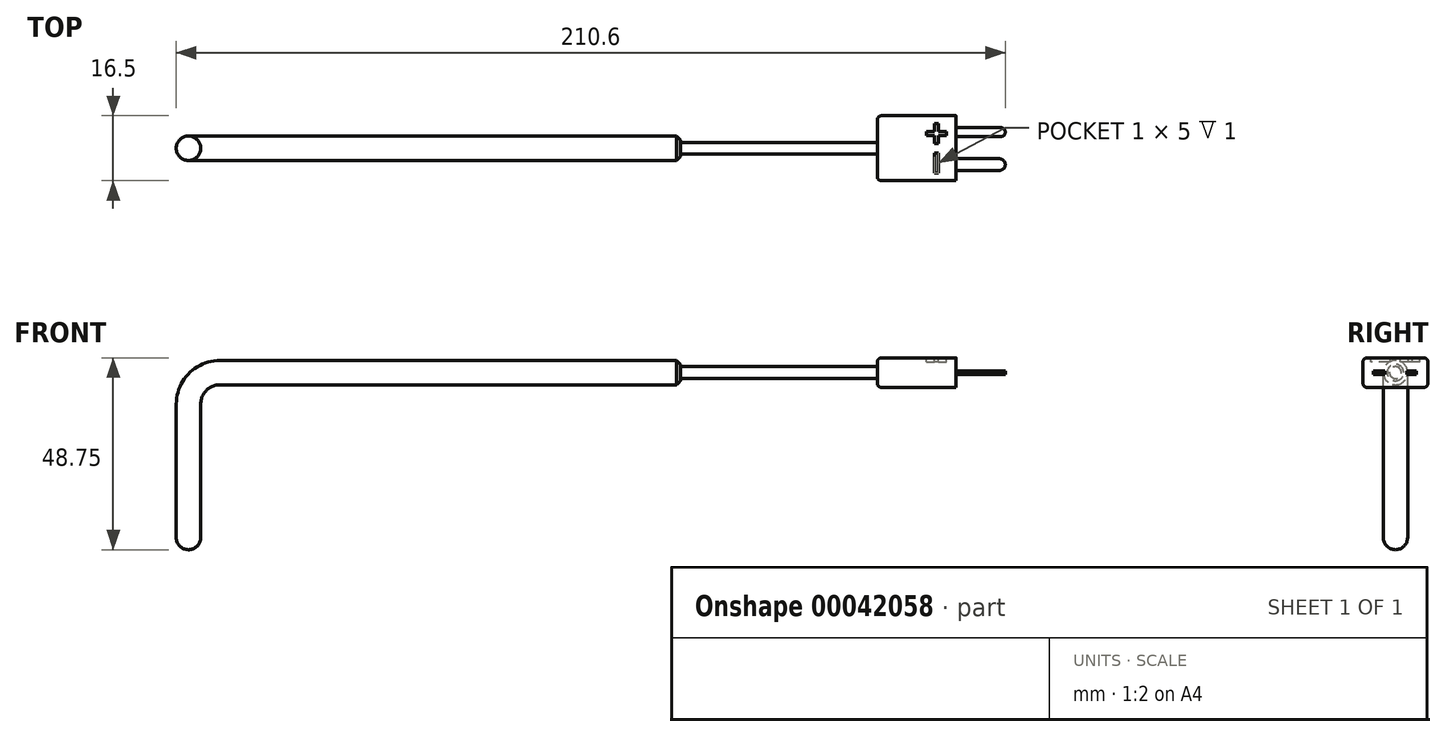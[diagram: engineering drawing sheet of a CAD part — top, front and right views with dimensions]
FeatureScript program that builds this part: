
annotation { "Feature Type Name" : "Feature", "Feature Type Description" : "" }
export const myFeature = defineFeature(function(context is Context, id is Id, definition is map)
    precondition{}
    {
        {
            var Q0;
            Q0=qCreatedBy(makeId("Front.planeOp"),FACE);
            var sketch = newSketch(context, id + "F0", { "sketchPlane" : qUnion([Q0])});
            skLineSegment(sketch, "E0", {"start": v(0, 0) * mm, "end": v(0, 37) * mm});
            skLineSegment(sketch, "E1", {"start": v(8, 45) * mm, "end": v(125, 45) * mm});
            skPoint(sketch, "E2.visualSharp", {"position": v(0, 45) * mm});
            skArc(sketch, "E2.filletArc", {"start": v(8, 45) * mm, "mid": v(2.34, 42.66) * mm, "end": v(0, 37) * mm});
            skSolve(sketch);
        }
        {
            var Q0;
            Q0=qCreatedBy(makeId("Top.planeOp"),FACE);
            var sketch = newSketch(context, id + "F1", { "sketchPlane" : qUnion([Q0])});
            skCircle(sketch, "E3", {"center": v(0, 0) * mm, "radius": 3.1 * mm});
            skSolve(sketch);
        }
        {
            var Q0;
            Q0=makeQuery(id+"F1.imprint","IMPRINT",FACE,{"disambiguationData":[TD([[makeQuery(id+"F1.imprint","IMPRINT",EDGE,{"derivedFrom":sQuery(id+"F1.wireOp",EDGE,"E3")}),1.0]])]});
            var Q1;
            Q1=sQuery(id+"F0.wireOp",EDGE,"E0");
            var Q2;
            Q2=sQuery(id+"F0.wireOp",EDGE,"E2.filletArc");
            var Q3;
            Q3=sQuery(id+"F0.wireOp",EDGE,"E1");
            sweep(context, id + "F2", {"profiles" : qUnion([Q0]), "path" : qUnion([Q1, Q2, Q3])});
        }
        {
            var Q0;
            Q0=makeQuery(id+"F2.opSweep","CAP_FACE",FACE,{"disambiguationData":[OSD([sQuery(id+"F0.wireOp",VERTEX,"E0.start"),sQuery(id+"F1.wireOp",EDGE,"E3")])],"isStart":true});
            fillet(context, id + "F3", {"entities" : qUnion([Q0]), "radius" : 3.1 * mm, "tangentPropagation" : true, "allowEdgeOverflow" : false});
        }
        {
            var Q0;
            Q0=makeQuery(id+"F2.opSweep","CAP_FACE",FACE,{"disambiguationData":[OSD([sQuery(id+"F0.wireOp",VERTEX,"E1.end"),sQuery(id+"F1.wireOp",EDGE,"E3")])],"isStart":false});
            var sketch = newSketch(context, id + "F4", { "sketchPlane" : qUnion([Q0])});
            skCircle(sketch, "E4", {"center": v(0, 45) * mm, "radius": 1.5 * mm});
            skSolve(sketch);
        }
        {
            var Q0;
            Q0=makeQuery(id+"F4.imprint","IMPRINT",FACE,{"disambiguationData":[TD([[makeQuery(id+"F4.imprint","IMPRINT",EDGE,{"derivedFrom":sQuery(id+"F4.wireOp",EDGE,"E4")}),1.0]])]});
            extrude(context, id + "F5", {"entities" : qUnion([Q0]), "depth" : 50 * mm});
        }
        {
            var Q0;
            Q0=makeQuery(id+"F2.opSweep","CAP_EDGE",EDGE,{"disambiguationData":[OSD([sQuery(id+"F0.wireOp",VERTEX,"E1.end"),sQuery(id+"F1.wireOp",EDGE,"E3")])],"isStart":false});
            chamfer(context, id + "F6", {"entities" : qUnion([Q0]), "width" : 1 * mm, "tangentPropagation" : true});
        }
        {
            var Q0;
            Q0=makeQuery(id+"F5.opExtrude","CAP_FACE",FACE,{"disambiguationData":[OSD([sQuery(id+"F4.wireOp",EDGE,"E4")])],"isStart":false});
            var sketch = newSketch(context, id + "F7", { "sketchPlane" : qUnion([Q0])});
            skLineSegment(sketch, "E5.rect.bottom", {"start": v(8.25, 48.75) * mm, "end": v(-8.25, 48.75) * mm});
            skLineSegment(sketch, "E5.rect.top", {"start": v(8.25, 41.25) * mm, "end": v(-8.25, 41.25) * mm});
            skLineSegment(sketch, "E5.rect.left", {"start": v(8.25, 48.75) * mm, "end": v(8.25, 41.25) * mm});
            skLineSegment(sketch, "E5.rect.right", {"start": v(-8.25, 48.75) * mm, "end": v(-8.25, 41.25) * mm});
            skPoint(sketch, "E5.rect.middle", {"position": v(0, 45) * mm});
            skSolve(sketch);
        }
        {
            var Q0;
            Q0=makeQuery(id+"F7.imprint","IMPRINT",FACE,{"disambiguationData":[TD([[makeQuery(id+"F7.imprint","IMPRINT",EDGE,{"derivedFrom":makeQuery(id+"F5.opExtrude","CAP_EDGE",EDGE,{"disambiguationData":[OSD([sQuery(id+"F4.wireOp",EDGE,"E4")])],"isStart":false})}),1.0]])]});
            var Q1;
            Q1=makeQuery(id+"F7.imprint","IMPRINT",FACE,{"disambiguationData":[TD([[makeQuery(id+"F7.imprint","IMPRINT",EDGE,{"derivedFrom":sQuery(id+"F7.wireOp",EDGE,"E5.rect.bottom")}),1.0]])]});
            extrude(context, id + "F8", {"entities" : qUnion([Q0, Q1]), "operationType" : NewBodyOperationType.ADD, "depth" : 20 * mm});
        }
        {
            var Q0;
            Q0=makeQuery(id+"F8.opExtrude","CAP_FACE",FACE,{"disambiguationData":[OSD([sQuery(id+"F7.wireOp",EDGE,"E5.rect.bottom"),sQuery(id+"F7.wireOp",EDGE,"E5.rect.top"),sQuery(id+"F7.wireOp",EDGE,"E5.rect.left"),sQuery(id+"F7.wireOp",EDGE,"E5.rect.right")])],"isStart":false});
            var sketch = newSketch(context, id + "F9", { "sketchPlane" : qUnion([Q0])});
            skLineSegment(sketch, "E6", {"start": v(-8.25, 45) * mm, "end": v(8.25, 45) * mm, "construction": true});
            skLineSegment(sketch, "E7", {"start": v(0, 48.75) * mm, "end": v(0, 41.25) * mm, "construction": true});
            skLineSegment(sketch, "E8.rect.bottom", {"start": v(-2.65, 45.45) * mm, "end": v(-5.65, 45.45) * mm});
            skLineSegment(sketch, "E8.rect.top", {"start": v(-2.65, 44.55) * mm, "end": v(-5.65, 44.55) * mm});
            skLineSegment(sketch, "E8.rect.left", {"start": v(-2.65, 45.45) * mm, "end": v(-2.65, 44.55) * mm});
            skLineSegment(sketch, "E8.rect.right", {"start": v(-5.65, 45.45) * mm, "end": v(-5.65, 44.55) * mm});
            skPoint(sketch, "E8.rect.middle", {"position": v(-4.15, 45) * mm});
            skLineSegment(sketch, "E9.rect.bottom", {"start": v(5.25, 45.45) * mm, "end": v(2.95, 45.45) * mm});
            skLineSegment(sketch, "E9.rect.top", {"start": v(5.25, 44.55) * mm, "end": v(2.95, 44.55) * mm});
            skLineSegment(sketch, "E9.rect.left", {"start": v(5.25, 45.45) * mm, "end": v(5.25, 44.55) * mm});
            skLineSegment(sketch, "E9.rect.right", {"start": v(2.95, 45.45) * mm, "end": v(2.95, 44.55) * mm});
            skPoint(sketch, "E9.rect.middle", {"position": v(4.1, 45) * mm});
            skSolve(sketch);
        }
        {
            var Q0;
            Q0=makeQuery(id+"F9.imprint","IMPRINT",FACE,{"disambiguationData":[TD([[makeQuery(id+"F9.imprint","IMPRINT",EDGE,{"derivedFrom":sQuery(id+"F9.wireOp",EDGE,"E8.rect.bottom")}),1.0]])]});
            var Q1;
            Q1=makeQuery(id+"F9.imprint","IMPRINT",FACE,{"disambiguationData":[TD([[makeQuery(id+"F9.imprint","IMPRINT",EDGE,{"derivedFrom":sQuery(id+"F9.wireOp",EDGE,"E9.rect.bottom")}),1.0]])]});
            extrude(context, id + "F10", {"entities" : qUnion([Q0, Q1]), "depth" : 12.5 * mm});
        }
        {
            var Q0;
            Q0=makeQuery(id+"F8.opExtrude","SWEPT_EDGE",EDGE,{"disambiguationData":[OSD([sQuery(id+"F7.wireOp",EDGE,"E5.rect.bottom"),sQuery(id+"F7.wireOp",EDGE,"E5.rect.right")])]});
            var Q1;
            Q1=makeQuery(id+"F8.opExtrude","CAP_EDGE",EDGE,{"disambiguationData":[OSD([sQuery(id+"F7.wireOp",EDGE,"E5.rect.bottom")])],"isStart":true});
            var Q2;
            Q2=makeQuery(id+"F8.opExtrude","SWEPT_EDGE",EDGE,{"disambiguationData":[OSD([sQuery(id+"F7.wireOp",EDGE,"E5.rect.bottom"),sQuery(id+"F7.wireOp",EDGE,"E5.rect.left")])]});
            var Q3;
            Q3=makeQuery(id+"F8.opExtrude","CAP_EDGE",EDGE,{"disambiguationData":[OSD([sQuery(id+"F7.wireOp",EDGE,"E5.rect.left")])],"isStart":true});
            var Q4;
            Q4=makeQuery(id+"F8.opExtrude","SWEPT_EDGE",EDGE,{"disambiguationData":[OSD([sQuery(id+"F7.wireOp",EDGE,"E5.rect.top"),sQuery(id+"F7.wireOp",EDGE,"E5.rect.left")])]});
            var Q5;
            Q5=makeQuery(id+"F8.opExtrude","CAP_EDGE",EDGE,{"disambiguationData":[OSD([sQuery(id+"F7.wireOp",EDGE,"E5.rect.top")])],"isStart":true});
            var Q6;
            Q6=makeQuery(id+"F8.opExtrude","SWEPT_EDGE",EDGE,{"disambiguationData":[OSD([sQuery(id+"F7.wireOp",EDGE,"E5.rect.top"),sQuery(id+"F7.wireOp",EDGE,"E5.rect.right")])]});
            var Q7;
            Q7=makeQuery(id+"F8.opExtrude","CAP_EDGE",EDGE,{"disambiguationData":[OSD([sQuery(id+"F7.wireOp",EDGE,"E5.rect.right")])],"isStart":true});
            fillet(context, id + "F11", {"entities" : qUnion([Q0, Q1, Q2, Q3, Q4, Q5, Q6, Q7]), "radius" : 1 * mm, "tangentPropagation" : true, "allowEdgeOverflow" : false});
        }
        {
            var Q0;
            Q0=makeQuery(id+"F10.opExtrude","CAP_EDGE",EDGE,{"disambiguationData":[OSD([sQuery(id+"F9.wireOp",EDGE,"E8.rect.left")])],"isStart":false});
            var Q1;
            Q1=makeQuery(id+"F10.opExtrude","CAP_EDGE",EDGE,{"disambiguationData":[OSD([sQuery(id+"F9.wireOp",EDGE,"E8.rect.right")])],"isStart":false});
            fillet(context, id + "F12", {"entities" : qUnion([Q0, Q1]), "radius" : 1.5 * mm, "tangentPropagation" : true, "allowEdgeOverflow" : false});
        }
        {
            var Q0;
            Q0=makeQuery(id+"F10.opExtrude","CAP_EDGE",EDGE,{"disambiguationData":[OSD([sQuery(id+"F9.wireOp",EDGE,"E9.rect.left")])],"isStart":false});
            var Q1;
            Q1=makeQuery(id+"F10.opExtrude","CAP_EDGE",EDGE,{"disambiguationData":[OSD([sQuery(id+"F9.wireOp",EDGE,"E9.rect.right")])],"isStart":false});
            fillet(context, id + "F13", {"entities" : qUnion([Q0, Q1]), "radius" : 1.15 * mm, "tangentPropagation" : true, "allowEdgeOverflow" : false});
        }
        {
            var Q0;
            Q0=makeQuery(id+"F8.opExtrude","SWEPT_FACE",FACE,{"disambiguationData":[OSD([sQuery(id+"F7.wireOp",EDGE,"E5.rect.bottom")])]});
            var sketch = newSketch(context, id + "F14", { "sketchPlane" : qUnion([Q0])});
            skLineSegment(sketch, "E10.rect.bottom", {"start": v(190.5, -1.25) * mm, "end": v(189.5, -1.25) * mm});
            skLineSegment(sketch, "E10.rect.top", {"start": v(190.5, -6.25) * mm, "end": v(189.5, -6.25) * mm});
            skLineSegment(sketch, "E10.rect.left", {"start": v(190.5, -1.25) * mm, "end": v(190.5, -6.25) * mm});
            skLineSegment(sketch, "E10.rect.right", {"start": v(189.5, -1.25) * mm, "end": v(189.5, -6.25) * mm});
            skPoint(sketch, "E10.rect.middle", {"position": v(190, -3.75) * mm});
            skLineSegment(sketch, "E11.rect.bottom", {"start": v(190.5, 6.25) * mm, "end": v(189.5, 6.25) * mm});
            skLineSegment(sketch, "E11.rect.top", {"start": v(190.5, 1.25) * mm, "end": v(189.5, 1.25) * mm});
            skLineSegment(sketch, "E11.rect.left", {"start": v(190.5, 6.25) * mm, "end": v(190.5, 1.25) * mm});
            skLineSegment(sketch, "E11.rect.right", {"start": v(189.5, 6.25) * mm, "end": v(189.5, 1.25) * mm});
            skPoint(sketch, "E11.rect.middle", {"position": v(190, 3.75) * mm});
            skPoint(sketch, "E11.rect.middle.positionSnap0", {"position": v(190, -1.25) * mm});
            skPoint(sketch, "E11.rect.centerSnap0", {"position": v(190, -1.25) * mm});
            skLineSegment(sketch, "E12.rect.bottom", {"start": v(187.5, 4.25) * mm, "end": v(192.5, 4.25) * mm});
            skLineSegment(sketch, "E12.rect.top", {"start": v(187.5, 3.25) * mm, "end": v(192.5, 3.25) * mm});
            skLineSegment(sketch, "E12.rect.left", {"start": v(187.5, 4.25) * mm, "end": v(187.5, 3.25) * mm});
            skLineSegment(sketch, "E12.rect.right", {"start": v(192.5, 4.25) * mm, "end": v(192.5, 3.25) * mm});
            skSolve(sketch);
        }
        {
            var Q0;
            Q0=makeQuery(id+"F14.imprint","IMPRINT",FACE,{"disambiguationData":[TD([[makeQuery(id+"F14.imprint","IMPRINT",EDGE,{"derivedFrom":sQuery(id+"F14.wireOp",EDGE,"E10.rect.bottom")}),1.0]])]});
            var Q1;
            {var subQ5=sQuery(id+"F14.wireOp",EDGE,"E11.rect.bottom");Q1=makeQuery(id+"F14.imprint","IMPRINT",FACE,{"disambiguationData":[TD([[makeQuery(id+"F14.imprint","IMPRINT",EDGE,{"derivedFrom":subQ5}),1.0]])]});}
            var Q2;
            {var subQ0=sQuery(id+"F14.wireOp",EDGE,"E12.rect.right");Q2=makeQuery(id+"F14.imprint","IMPRINT",FACE,{"disambiguationData":[TD([[makeQuery(id+"F14.imprint","IMPRINT",EDGE,{"derivedFrom":subQ0}),-1.0]])]});}
            var Q3;
            {var subQ3=sQuery(id+"F14.wireOp",EDGE,"E11.rect.left");var subQ5=sQuery(id+"F14.wireOp",EDGE,"E12.rect.bottom");var subQ7=makeQuery(id+"F14.imprint","INTERSECT",VERTEX,{"derivedFrom":[subQ3,subQ5]});Q3=makeQuery(id+"F14.imprint","IMPRINT",FACE,{"disambiguationData":[TD([[makeQuery(id+"F14.imprint","IMPRINT",EDGE,{"disambiguationData":[TD([[subQ7,-1.0]])],"derivedFrom":subQ3}),-1.0]])]});}
            var Q4;
            {var subQ5=sQuery(id+"F14.wireOp",EDGE,"E11.rect.top");Q4=makeQuery(id+"F14.imprint","IMPRINT",FACE,{"disambiguationData":[TD([[makeQuery(id+"F14.imprint","IMPRINT",EDGE,{"derivedFrom":subQ5}),-1.0]])]});}
            var Q5;
            {var subQ0=sQuery(id+"F14.wireOp",EDGE,"E12.rect.left");Q5=makeQuery(id+"F14.imprint","IMPRINT",FACE,{"disambiguationData":[TD([[makeQuery(id+"F14.imprint","IMPRINT",EDGE,{"derivedFrom":subQ0}),1.0]])]});}
            extrude(context, id + "F15", {"entities" : qUnion([Q0, Q1, Q2, Q3, Q4, Q5]), "operationType" : NewBodyOperationType.REMOVE, "oppositeDirection" : true, "depth" : 1 * mm});
        }
    });
